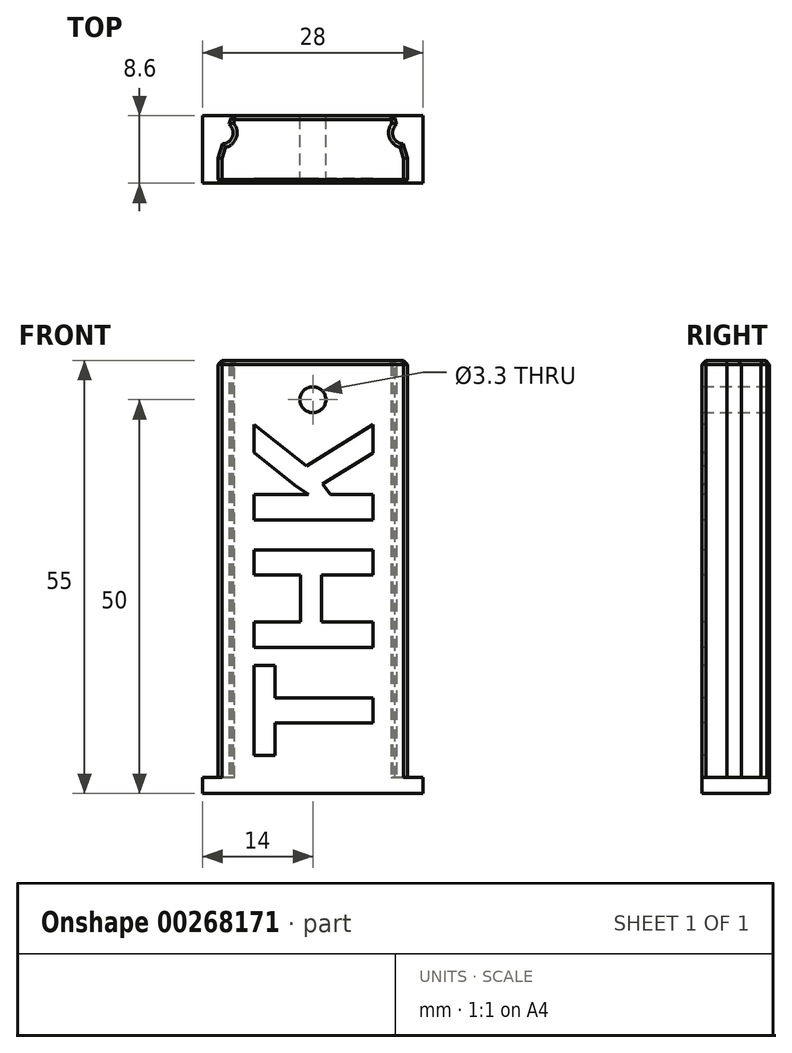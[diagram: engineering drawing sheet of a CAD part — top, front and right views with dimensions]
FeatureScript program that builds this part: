
annotation { "Feature Type Name" : "Feature", "Feature Type Description" : "" }
export const myFeature = defineFeature(function(context is Context, id is Id, definition is map)
    precondition{}
    {
        {
            var Q0;
            Q0=qCreatedBy(makeId("Top.planeOp"),FACE);
            var sketch = newSketch(context, id + "F0", { "sketchPlane" : qUnion([Q0])});
            skLineSegment(sketch, "E0.bottom", {"start": v(14, -4.3) * mm, "end": v(-14, -4.3) * mm});
            skLineSegment(sketch, "E0.top", {"start": v(14, 4.3) * mm, "end": v(-14, 4.3) * mm});
            skLineSegment(sketch, "E0.left", {"start": v(14, -4.3) * mm, "end": v(14, 4.3) * mm});
            skLineSegment(sketch, "E0.right", {"start": v(-14, -4.3) * mm, "end": v(-14, 4.3) * mm});
            skPoint(sketch, "E0.middle", {"position": v(0, 0) * mm});
            skSolve(sketch);
        }
        {
            var Q0;
            Q0=qSketchRegion(id+"F0",true);
            extrude(context, id + "F1", {"entities" : qUnion([Q0]), "depth" : 2 * mm});
        }
        {
            var Q0;
            Q0=makeQuery(id+"F1.opExtrude","CAP_FACE",FACE,{"disambiguationData":[OSD([sQuery(id+"F0.wireOp",EDGE,"E0.bottom"),sQuery(id+"F0.wireOp",EDGE,"E0.top"),sQuery(id+"F0.wireOp",EDGE,"E0.left"),sQuery(id+"F0.wireOp",EDGE,"E0.right")])],"isStart":false});
            var sketch = newSketch(context, id + "F2", { "sketchPlane" : qUnion([Q0])});
            skLineSegment(sketch, "E1", {"start": v(-10.3, 4.3) * mm, "end": v(10.3, 4.3) * mm});
            skLineSegment(sketch, "E2", {"start": v(-12.03, -4.3) * mm, "end": v(12.03, -4.3) * mm});
            skLineSegment(sketch, "E3", {"start": v(-12.03, -4.3) * mm, "end": v(-12.03, -1.1) * mm});
            skLineSegment(sketch, "E4", {"start": v(12.02, -4.3) * mm, "end": v(12.02, -1.1) * mm});
            skLineSegment(sketch, "E5", {"start": v(-12.03, -1.1) * mm, "end": v(-11.45, 0.71) * mm});
            skLineSegment(sketch, "E6", {"start": v(10.3, 4.3) * mm, "end": v(10.65, 3.2) * mm});
            skPoint(sketch, "E7", {"position": v(-11.06, 1.92) * mm});
            skArc(sketch, "E8", {"start": v(-11.45, 0.71) * mm, "mid": v(-10.2, 1.69) * mm, "end": v(-10.65, 3.2) * mm});
            skLineSegment(sketch, "E9.trimOffspring", {"start": v(-10.65, 3.2) * mm, "end": v(-10.3, 4.3) * mm});
            skArc(sketch, "E10", {"start": v(10.65, 3.2) * mm, "mid": v(10.2, 1.69) * mm, "end": v(11.45, 0.71) * mm});
            skLineSegment(sketch, "E11.trimOffspring", {"start": v(11.45, 0.71) * mm, "end": v(12.03, -1.1) * mm});
            skSolve(sketch);
        }
        {
            var Q0;
            Q0=qSketchRegion(id+"F2",true);
            extrude(context, id + "F3", {"entities" : qUnion([Q0]), "operationType" : NewBodyOperationType.ADD, "depth" : 53 * mm});
        }
        {
            var Q0;
            Q0=makeQuery(id+"F3.opExtrude","SWEPT_FACE",FACE,{"disambiguationData":[OSD([sQuery(id+"F2.wireOp",EDGE,"E1")])]});
            var sketch = newSketch(context, id + "F4", { "sketchPlane" : qUnion([Q0])});
            skCircle(sketch, "E12", {"center": v(0, 50) * mm, "radius": 1.65 * mm});
            skSolve(sketch);
        }
        {
            var Q0;
            Q0=qSketchRegion(id+"F4",true);
            extrude(context, id + "F5", {"entities" : qUnion([Q0]), "operationType" : NewBodyOperationType.REMOVE, "endBound" : BoundingType.THROUGH_ALL, "oppositeDirection" : true, "depth" : 25 * mm});
        }
        {
            var Q0;
            Q0=makeQuery(id+"F3.opExtrude","CAP_FACE",FACE,{"disambiguationData":[OSD([sQuery(id+"F2.wireOp",EDGE,"E1"),sQuery(id+"F2.wireOp",EDGE,"E2"),sQuery(id+"F2.wireOp",EDGE,"vByZBdFE-P4d9-4Vax-7Tm4-q66zOkJRXM8e"),sQuery(id+"F2.wireOp",EDGE,"AEALtSVL-k1z2-yZ09-4UEp-tEW5cBDfWY5V"),sQuery(id+"F2.wireOp",EDGE,"bxKjowka-Hegi-xfs2-sxSI-ibNg6VljLOrK"),sQuery(id+"F2.wireOp",EDGE,"fDAdd9wD-Ftge-8WgB-mxXS-h6YQjjJBvm8D"),sQuery(id+"F2.wireOp",EDGE,"Rscrgpam-4JoX-izmN-PVr4-PEdRK0yLe6vD"),sQuery(id+"F2.wireOp",EDGE,"88Kh43rL-8lwz-HEh3-Ppw5-ub2MFPE0m77Y")])],"isStart":false});
            var Q1;
            Q1=makeQuery(id+"F3.opExtrude","SWEPT_EDGE",EDGE,{"disambiguationData":[OSD([sQuery(id+"F0.wireOp",EDGE,"E0.top"),sQuery(id+"F2.wireOp",EDGE,"E1"),sQuery(id+"F2.wireOp",EDGE,"bxKjowka-Hegi-xfs2-sxSI-ibNg6VljLOrK")])]});
            var Q2;
            Q2=makeQuery(id+"F3.opExtrude","SWEPT_EDGE",EDGE,{"disambiguationData":[OSD([sQuery(id+"F0.wireOp",EDGE,"E0.top"),sQuery(id+"F2.wireOp",EDGE,"E1"),sQuery(id+"F2.wireOp",EDGE,"vByZBdFE-P4d9-4Vax-7Tm4-q66zOkJRXM8e")])]});
            var Q3;
            Q3=makeQuery(id+"F3.opExtrude","SWEPT_EDGE",EDGE,{"disambiguationData":[OSD([sQuery(id+"F0.wireOp",EDGE,"E0.bottom"),sQuery(id+"F2.wireOp",EDGE,"E2"),sQuery(id+"F2.wireOp",EDGE,"fDAdd9wD-Ftge-8WgB-mxXS-h6YQjjJBvm8D")])]});
            var Q4;
            Q4=makeQuery(id+"F3.opExtrude","SWEPT_EDGE",EDGE,{"disambiguationData":[OSD([sQuery(id+"F0.wireOp",EDGE,"E0.bottom"),sQuery(id+"F2.wireOp",EDGE,"E2"),sQuery(id+"F2.wireOp",EDGE,"AEALtSVL-k1z2-yZ09-4UEp-tEW5cBDfWY5V")])]});
            chamfer(context, id + "F6", {"entities" : qUnion([Q0, Q1, Q2, Q3, Q4]), "width" : .5 * mm, "tangentPropagation" : true});
        }
        {
            var Q0;
            Q0=makeQuery(id+"F3.boolean.opBoolean","MERGE",FACE,{"derivedFrom":[makeQuery(id+"F1.opExtrude","SWEPT_FACE",FACE,{"disambiguationData":[OSD([sQuery(id+"F0.wireOp",EDGE,"E0.bottom")])]}),makeQuery(id+"F3.opExtrude","SWEPT_FACE",FACE,{"disambiguationData":[OSD([sQuery(id+"F2.wireOp",EDGE,"E2")])]})]});
            var sketch = newSketch(context, id + "F7", { "sketchPlane" : qUnion([Q0])});
            skText(sketch, "E13", { "text": "THK", "fontName": "OpenSans-Bold.ttf"});
            skPoint(sketch, "E14", {"position": v(0, 48.25) * mm});
            const initialGuessF7  = {"E13": [0.00762, 0.0044, 0, 1, 0.01523]};
            skSetInitialGuess(sketch, initialGuessF7);
            skSolve(sketch);
        }
        {
            var Q0;
            Q0=qSketchRegion(id+"F7",true);
            extrude(context, id + "F8", {"entities" : qUnion([Q0]), "operationType" : NewBodyOperationType.REMOVE, "oppositeDirection" : true, "depth" : .6 * mm});
        }
    });
